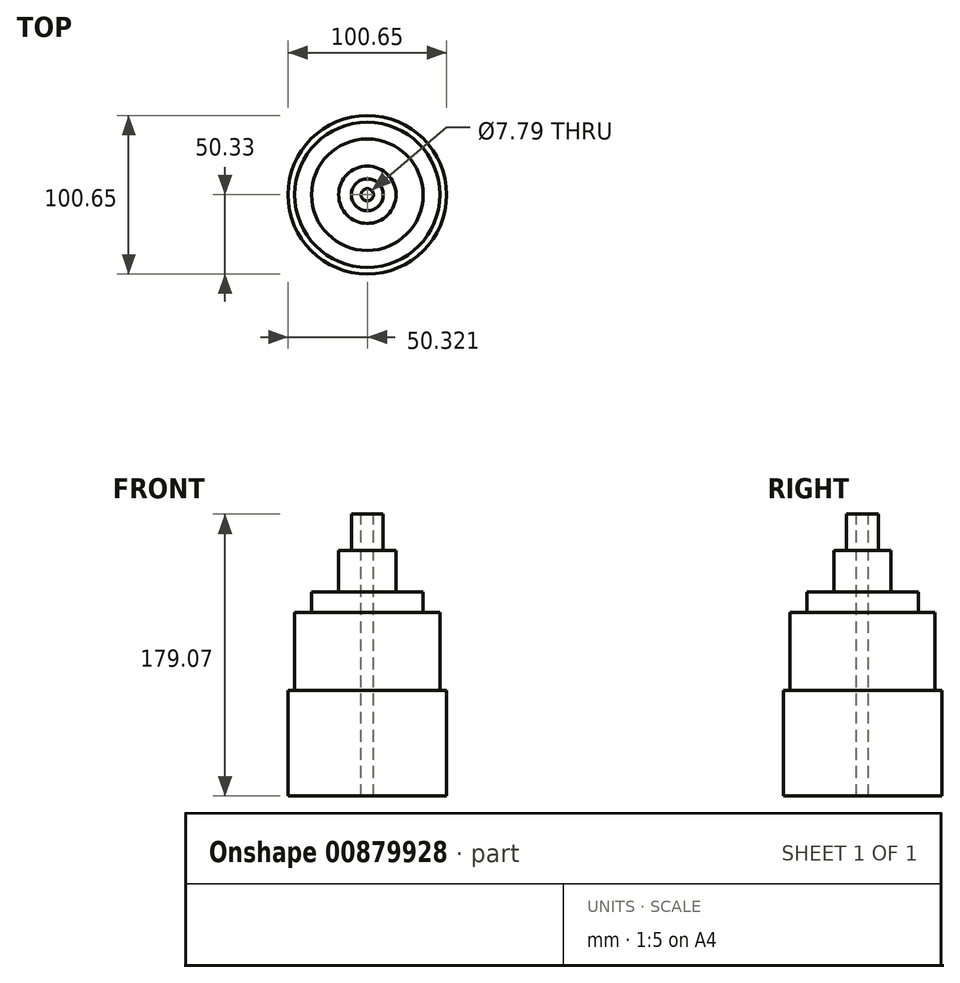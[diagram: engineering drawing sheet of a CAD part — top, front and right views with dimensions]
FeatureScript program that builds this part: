
annotation { "Feature Type Name" : "Feature", "Feature Type Description" : "" }
export const myFeature = defineFeature(function(context is Context, id is Id, definition is map)
    precondition{}
    {
        {
            var Q0;
            Q0=qCreatedBy(makeId("Top.planeOp"),FACE);
            var sketch = newSketch(context, id + "F0", { "sketchPlane" : qUnion([Q0])});
            skCircle(sketch, "E0", {"center": v(-71.73, 33.04) * mm, "radius": 50.33 * mm});
            skCircle(sketch, "E1", {"center": v(-71.73, 33.04) * mm, "radius": 46.1 * mm});
            skCircle(sketch, "E2", {"center": v(-71.73, 33.04) * mm, "radius": 35.43 * mm});
            skCircle(sketch, "E3", {"center": v(-71.73, 33.04) * mm, "radius": 18.2 * mm});
            skCircle(sketch, "E4", {"center": v(-71.73, 33.04) * mm, "radius": 10.12 * mm});
            skSolve(sketch);
        }
        {
            var Q0;
            Q0=makeQuery(id+"F0.imprint","IMPRINT",FACE,{"disambiguationData":[TD([[makeQuery(id+"F0.imprint","IMPRINT",EDGE,{"derivedFrom":sQuery(id+"F0.wireOp",EDGE,"E4")}),1.0]])]});
            extrude(context, id + "F1", {"entities" : qUnion([Q0]), "depth" : 179.07 * mm, "offsetDistance" : 25.4 * mm});
        }
        {
            var Q0;
            Q0=makeQuery(id+"F0.imprint","IMPRINT",FACE,{"disambiguationData":[TD([[makeQuery(id+"F0.imprint","IMPRINT",EDGE,{"derivedFrom":sQuery(id+"F0.wireOp",EDGE,"E3")}),1.0]])]});
            extrude(context, id + "F2", {"entities" : qUnion([Q0]), "operationType" : NewBodyOperationType.ADD, "depth" : 155.96 * mm, "offsetDistance" : 25.4 * mm});
        }
        {
            var Q0;
            Q0=makeQuery(id+"F0.imprint","IMPRINT",FACE,{"disambiguationData":[TD([[makeQuery(id+"F0.imprint","IMPRINT",EDGE,{"derivedFrom":sQuery(id+"F0.wireOp",EDGE,"E2")}),1.0]])]});
            extrude(context, id + "F3", {"entities" : qUnion([Q0]), "operationType" : NewBodyOperationType.ADD, "depth" : 129.54 * mm, "offsetDistance" : 25.4 * mm});
        }
        {
            var Q0;
            Q0=makeQuery(id+"F0.imprint","IMPRINT",FACE,{"disambiguationData":[TD([[makeQuery(id+"F0.imprint","IMPRINT",EDGE,{"derivedFrom":sQuery(id+"F0.wireOp",EDGE,"E1")}),1.0]])]});
            extrude(context, id + "F4", {"entities" : qUnion([Q0]), "operationType" : NewBodyOperationType.ADD, "depth" : 116.6 * mm, "offsetDistance" : 25.4 * mm});
        }
        {
            var Q0;
            Q0=makeQuery(id+"F0.imprint","IMPRINT",FACE,{"disambiguationData":[TD([[makeQuery(id+"F0.imprint","IMPRINT",EDGE,{"derivedFrom":sQuery(id+"F0.wireOp",EDGE,"E0")}),1.0]])]});
            extrude(context, id + "F5", {"entities" : qUnion([Q0]), "operationType" : NewBodyOperationType.ADD, "depth" : 67.06 * mm, "offsetDistance" : 25.4 * mm});
        }
        {
            var Q0;
            Q0=makeQuery(id+"F1.opExtrude","CAP_FACE",FACE,{"disambiguationData":[OSD([sQuery(id+"F0.wireOp",EDGE,"E4")])],"isStart":false});
            var sketch = newSketch(context, id + "F6", { "sketchPlane" : qUnion([Q0])});
            skCircle(sketch, "E5", {"center": v(-71.73, 33.04) * mm, "radius": 3.9 * mm});
            skSolve(sketch);
        }
        {
            var Q0;
            Q0 = qSketchRegion(id + "F6", true);
            extrude(context, id + "F7", {"entities" : qUnion([Q0]), "operationType" : NewBodyOperationType.REMOVE, "oppositeDirection" : true, "depth" : 411.23 * mm, "offsetDistance" : 25.4 * mm});
        }
    });
